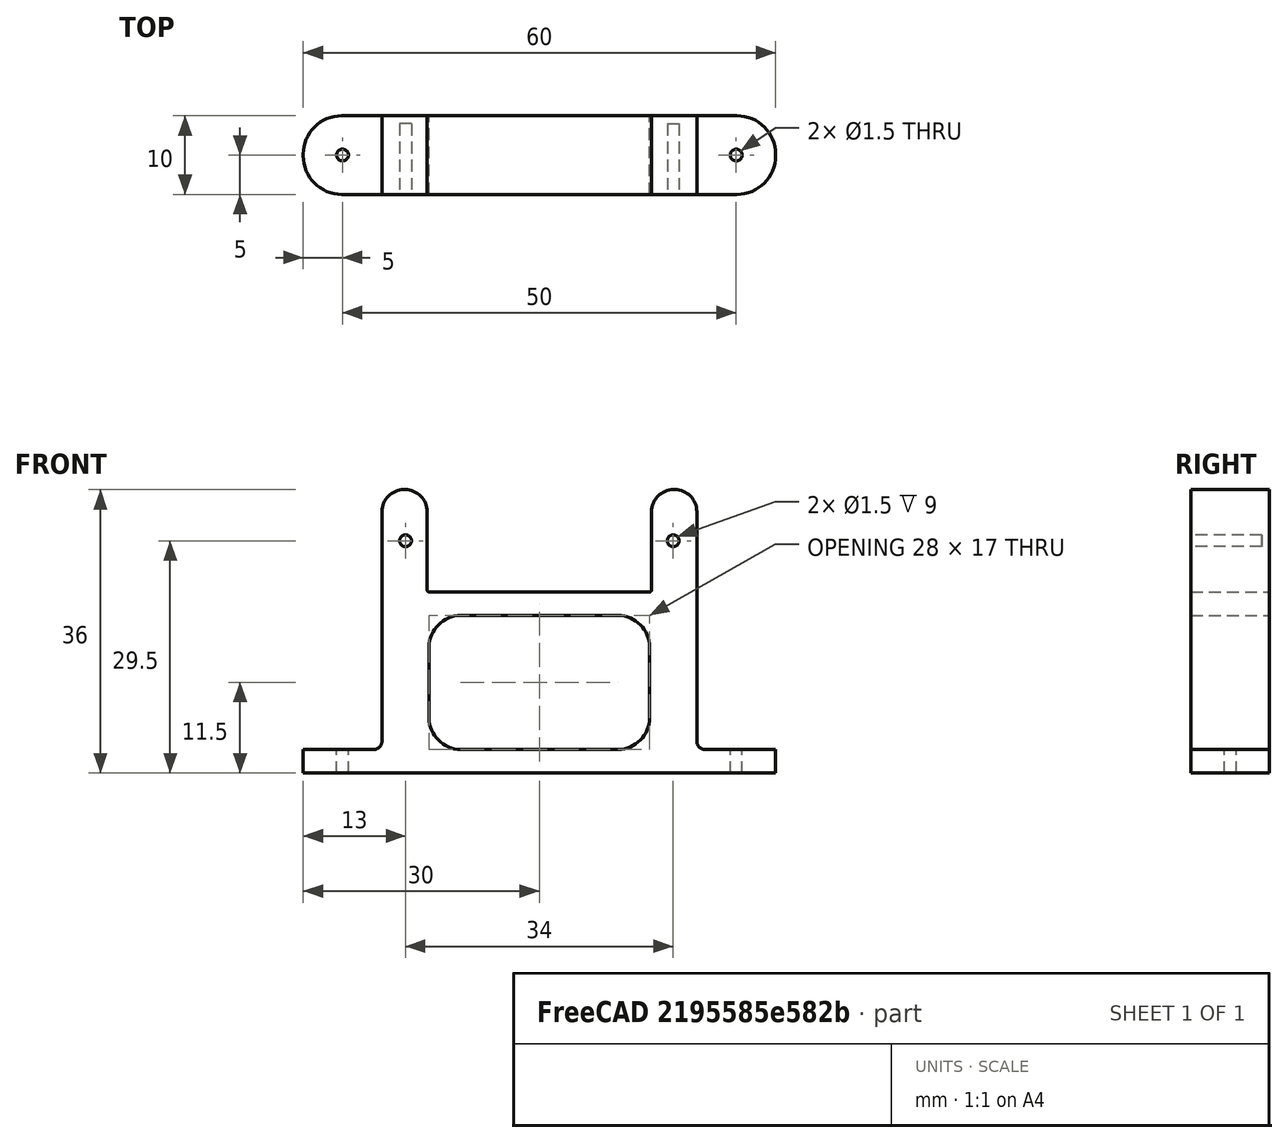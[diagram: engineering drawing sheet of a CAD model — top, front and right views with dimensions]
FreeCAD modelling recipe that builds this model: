
FCSTD DOCUMENT  (FreeCAD 0.16R6712 (Git))
Label: Soporte servo 13 x 28 horizontal
License: CreativeCommons Attribution
LicenseURL: http://creativecommons.org/licenses/by/4.0/
objects: Part::Box×4, Part::Mirroring×3, Part::Fillet×2, Part::MultiFuse×2, Part::Cylinder×2, Part::Offset×1, Part::Cut×1
note: 15 computed .brp shape members not serialized (recipe doc carries the construction recipe); baked Part::Feature solids carry a one-line shape summary decoded from their .brp

FEATURE [Part::Box] Box  label="Cubo base soporte"
  Height = 36
  Length = 40
  Placement = pos=(-20,0,0) rot=(0,0,1;0rad)
  Width = 10
FEATURE [Part::Box] Box001  label="Cubo servo 13x28x20"
  Height = 13
  Length = 28
  Placement = pos=(-14,-1.75,23.25) rot=(0,0,1;0rad)
  Width = 20
FEATURE [Part::Box] Box002  label="Cubo soporte lateral master"
  Height = 3
  Length = 10
  Placement = pos=(-30,0,0) rot=(0,0,1;0rad)
  Width = 10
FEATURE [Part::Fillet] Fillet
  Base = -> Box002
  Edges = 2 edges r=4.9: [Edge1,Edge3]
FEATURE [Part::Mirroring] Part__Mirroring  label="Fillet (Mirror #1)"
  Base = (0,0,0)
  Normal = (1,0,0)
  Source = -> Fillet
FEATURE [Part::Box] Box003  label="vaciado exceso de material"
  Height = 17
  Length = 28
  Placement = pos=(-14,-3,3) rot=(0,0,1;0rad)
  Width = 16
FEATURE [Part::MultiFuse] Fusion  label="Soporte macizo con aletas"
  Shapes = -> [Part__Mirroring,Fillet,Box]
FEATURE [Part::Cylinder] Cylinder  label="Hueco master tornillo servo"
  Angle = 360
  Height = 10
  Placement = pos=(-17,9,29.5) rot=(1,0,0;1.5708rad)
  Radius = 0.75
FEATURE [Part::Mirroring] Part__Mirroring001  label="Hueco master tornillo servo (Mirror #2)"
  Base = (0,0,0)
  Normal = (1,0,0)
  Source = -> Cylinder
FEATURE [Part::Offset] Offset  label=" offset hueco servo 13x28x20"
  Fill = false
  Intersection = false
  Join = 0
  Mode = 0
  SelfIntersection = false
  Source = -> Box001
  Value = 0.25
FEATURE [Part::Cylinder] Cylinder001  label="Hueco chinceta master"
  Angle = 360
  Height = 12
  Placement = pos=(-25,5,-5) rot=(0,0,1;0rad)
  Radius = 0.75
FEATURE [Part::Mirroring] Part__Mirroring002  label="Hueco chinceta master (Mirror #3)"
  Base = (0,0,0)
  Normal = (1,0,0)
  Source = -> Cylinder001
FEATURE [Part::MultiFuse] Fusion001  label="Fusion huecos"
  Shapes = -> [Box003,Part__Mirroring001,Cylinder,Offset,Cylinder001,Part__Mirroring002]
FEATURE [Part::Cut] Cut  label="soporte macizo menos huecos"
  Base = -> Fusion
  Tool = -> Fusion001
FEATURE [Part::Fillet] Fillet001  label="Soporte servo horizontal"
  Base = -> Cut
  Edges = 10 edges: [Edge2 r=2.8,Edge4 r=2.8,Edge42 r=1,Edge55 r=1,Edge57 r=2.8,Edge58 r=2.8,Edge67 r=4,Edge68 r=4,Edge69 r=4,Edge70 r=4]
